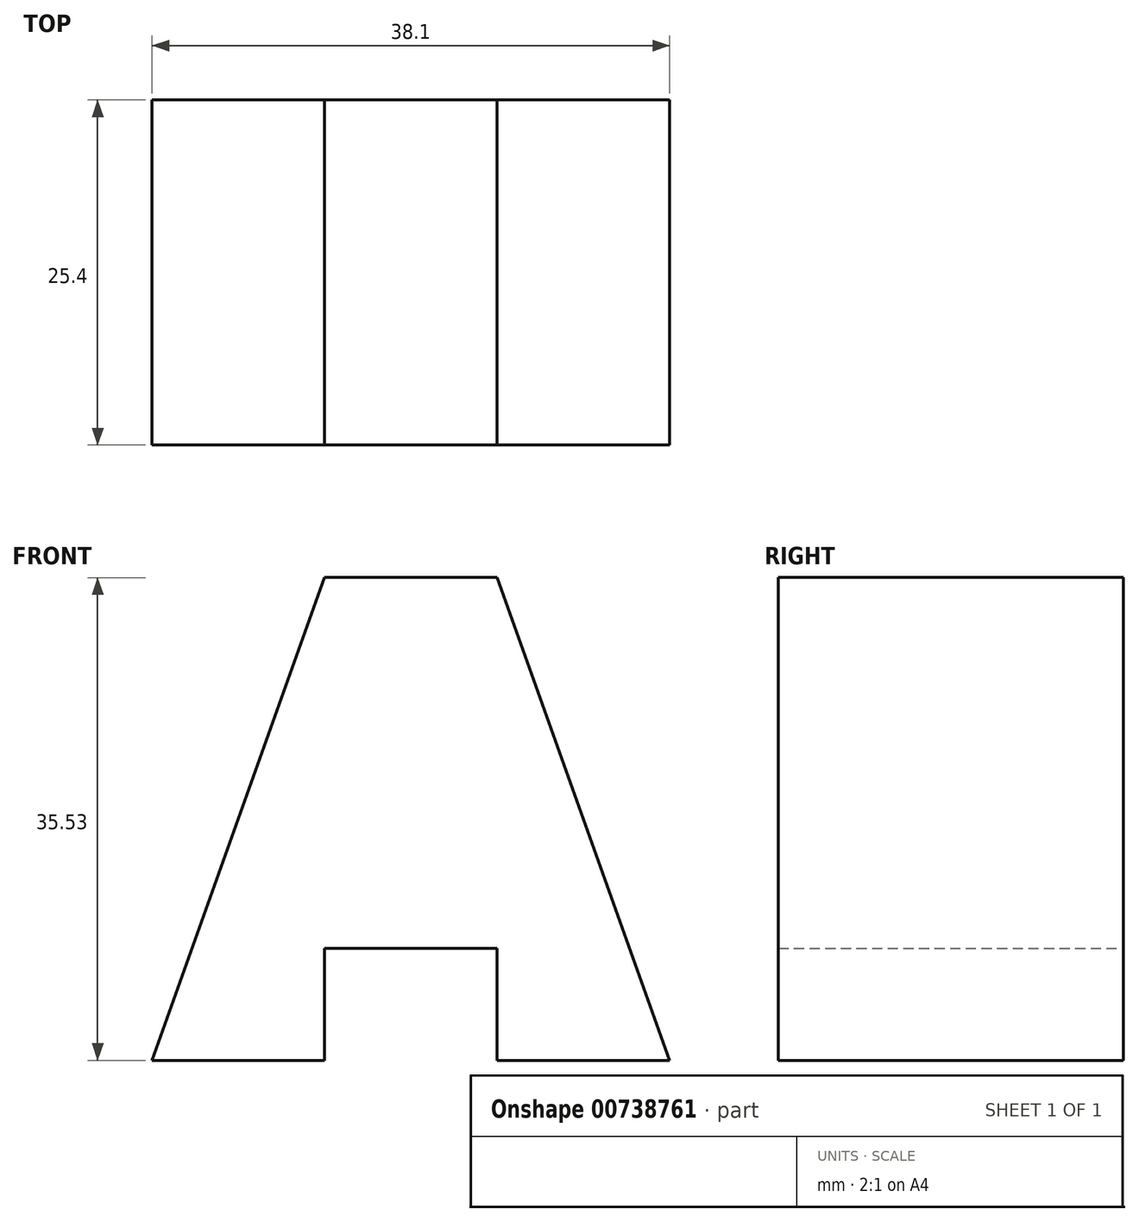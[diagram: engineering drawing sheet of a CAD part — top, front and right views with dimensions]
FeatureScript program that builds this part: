
annotation { "Feature Type Name" : "Feature", "Feature Type Description" : "" }
export const myFeature = defineFeature(function(context is Context, id is Id, definition is map)
    precondition{}
    {
        {
            var Q0;
            Q0=qCreatedBy(makeId("Front.planeOp"),FACE);
            var sketch = newSketch(context, id + "F0", { "sketchPlane" : qUnion([Q0])});
            skLineSegment(sketch, "E0", {"start": v(0, 0) * mm, "end": v(-12.7, 35.53) * mm});
            skLineSegment(sketch, "E1", {"start": v(-12.7, 35.53) * mm, "end": v(-25.4, 35.53) * mm});
            skLineSegment(sketch, "E2", {"start": v(-25.4, 35.53) * mm, "end": v(-38.1, 0) * mm});
            skLineSegment(sketch, "E3", {"start": v(-38.1, 0) * mm, "end": v(-25.4, 0) * mm});
            skLineSegment(sketch, "E4", {"start": v(-25.4, 0) * mm, "end": v(-25.4, 8.24) * mm});
            skLineSegment(sketch, "E5", {"start": v(-25.4, 8.24) * mm, "end": v(-12.7, 8.24) * mm});
            skLineSegment(sketch, "E6", {"start": v(-12.7, 8.24) * mm, "end": v(-12.7, 0) * mm});
            skLineSegment(sketch, "E7", {"start": v(-12.7, 0) * mm, "end": v(0, 0) * mm});
            skSolve(sketch);
        }
        {
            var Q0;
            Q0 = qSketchRegion(id + "F0", true);
            extrude(context, id + "F1", {"entities" : qUnion([Q0]), "depth" : 25.4 * mm, "offsetDistance" : 25.4 * mm});
        }
    });
